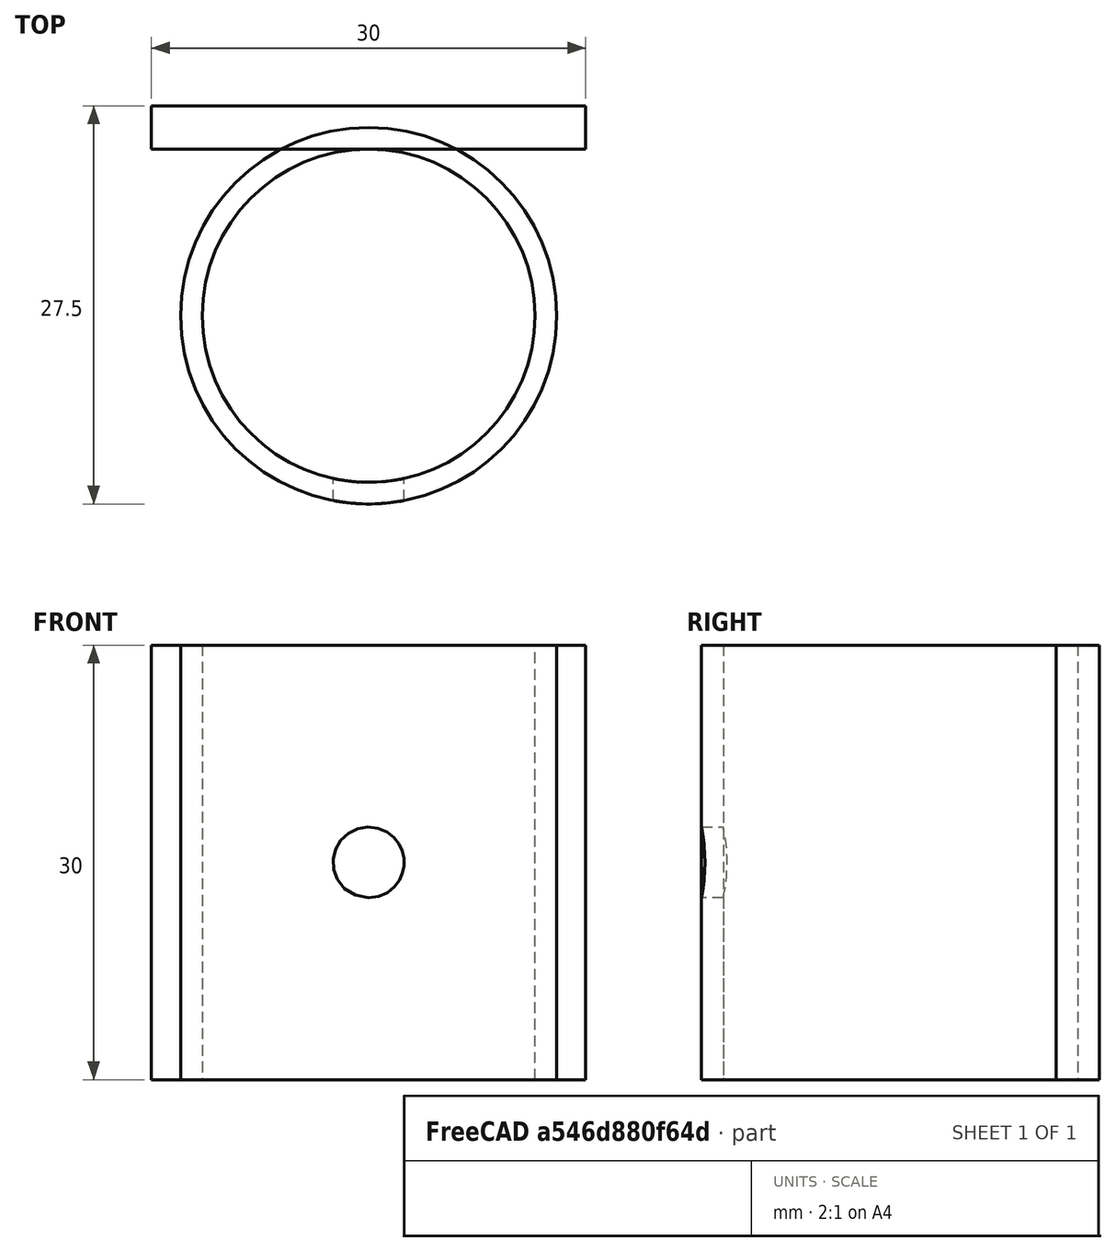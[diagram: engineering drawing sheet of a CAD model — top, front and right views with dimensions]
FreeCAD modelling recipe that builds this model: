
FCSTD DOCUMENT  (FreeCAD 0.21R33771 (Git))
Label: laserholder
License: All rights reserved
LicenseURL: https://en.wikipedia.org/wiki/All_rights_reserved
objects: Part::Compound×2, PartDesign::AdditiveCylinder×1, PartDesign::SubtractiveCylinder×1, PartDesign::Body×1, Part::Box×1, Part::Cylinder×1, Part::Cut×1
note: 10 computed .brp shape members not serialized (recipe doc carries the construction recipe); baked Part::Feature solids carry a one-line shape summary decoded from their .brp

FEATURE [PartDesign::AdditiveCylinder] Cylinder
  Angle = 360
  AttacherType = Attacher::AttachEngine3D
  FirstAngle = 0
  Height = 30
  Radius = 13
  SecondAngle = 0
FEATURE [PartDesign::SubtractiveCylinder] Cylinder001
  Angle = 360
  AttacherType = Attacher::AttachEngine3D
  BaseFeature = -> Cylinder
  FirstAngle = 0
  Height = 40
  Radius = 11.5
  SecondAngle = 0
FEATURE [PartDesign::Body] Body
  Group = -> [Cylinder,Cylinder001]
  Origin = -> Origin
  Tip = -> Cylinder001
FEATURE [Part::Compound] Compound
  Links = -> [Cylinder001]
FEATURE [Part::Box] Box  label="Cube"
  AttacherType = Attacher::AttachEngine3D
  Height = 30
  Length = 30
  Placement = pos=(-15,11.5,0) rot=(0,0,1;0rad)
  Width = 3
FEATURE [Part::Compound] Compound001
  Links = -> [Box,Compound]
FEATURE [Part::Cylinder] Cylinder002
  Angle = 360
  AttacherType = Attacher::AttachEngine3D
  FirstAngle = 0
  Height = 10
  Placement = pos=(0,-9,15) rot=(0.57735,0.57735,-0.57735;2.0944rad)
  Radius = 2.45
  SecondAngle = 0
FEATURE [Part::Cut] Cut
  Base = -> Compound001
  Tool = -> Cylinder002
